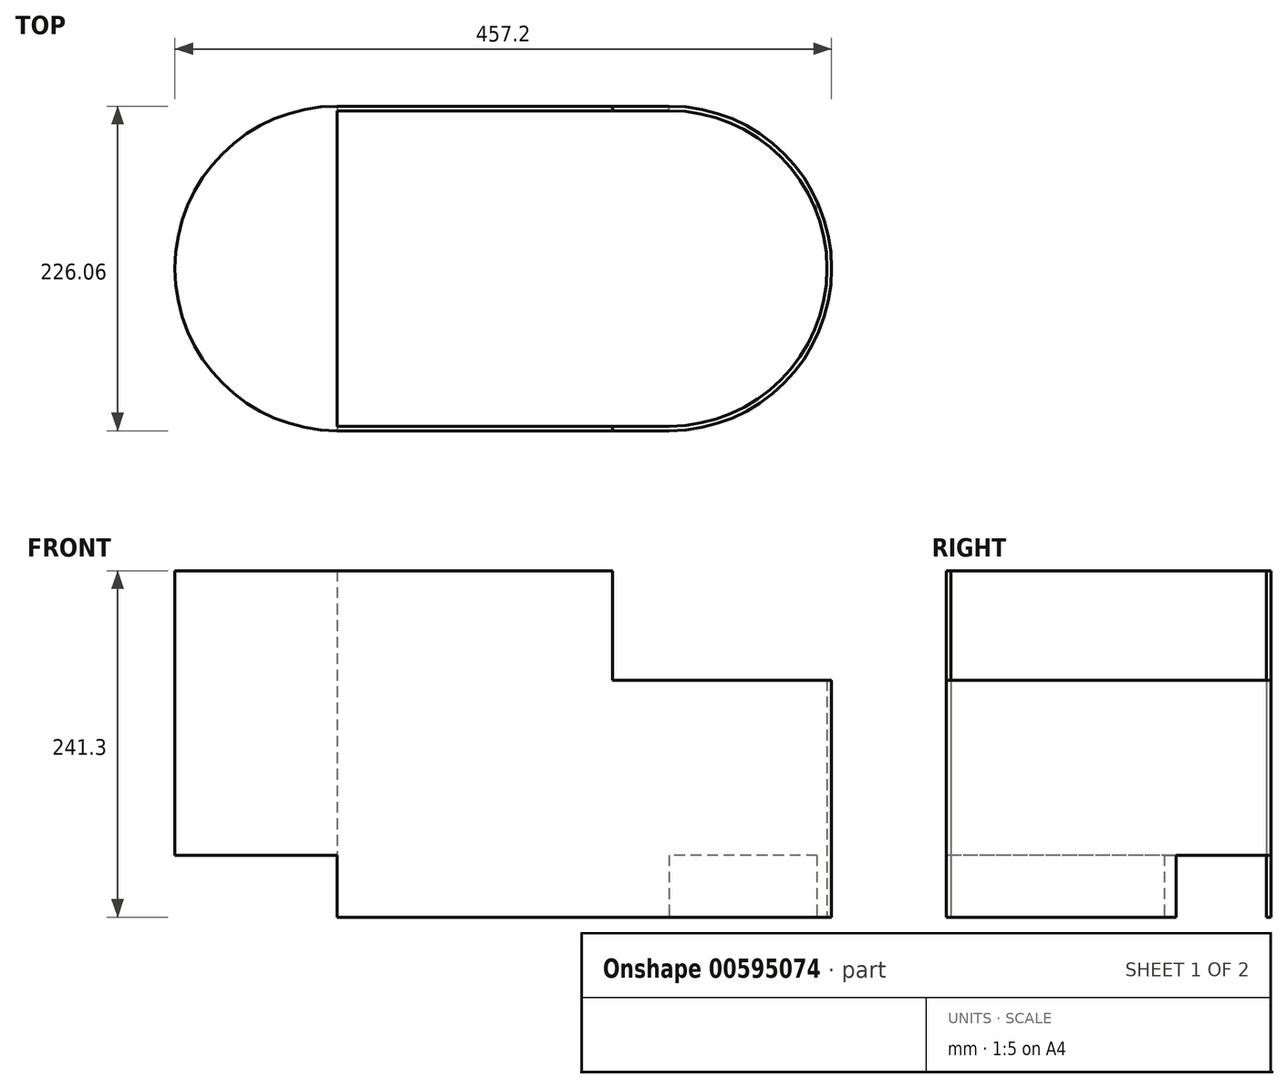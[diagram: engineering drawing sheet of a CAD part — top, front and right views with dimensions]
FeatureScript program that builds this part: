
annotation { "Feature Type Name" : "Feature", "Feature Type Description" : "" }
export const myFeature = defineFeature(function(context is Context, id is Id, definition is map)
    precondition{}
    {
        {
            var Q0;
            Q0=qCreatedBy(makeId("Top.planeOp"),FACE);
            var sketch = newSketch(context, id + "F0", { "sketchPlane" : qUnion([Q0])});
            skLineSegment(sketch, "E0.bottom", {"start": v(-173.03, 52.32) * mm, "end": v(58.1, 52.32) * mm});
            skLineSegment(sketch, "E0.top", {"start": v(-173.03, -173.74) * mm, "end": v(58.1, -173.74) * mm});
            skLineSegment(sketch, "E0.left", {"start": v(-173.03, 52.32) * mm, "end": v(-173.03, -173.74) * mm});
            skLineSegment(sketch, "E0.right", {"start": v(58.1, 52.32) * mm, "end": v(58.1, -173.74) * mm});
            skArc(sketch, "E1", {"start": v(58.1, -173.74) * mm, "mid": v(171.14, -60.71) * mm, "end": v(58.1, 52.32) * mm});
            skArc(sketch, "E2", {"start": v(-173.03, 52.32) * mm, "mid": v(-286.06, -60.71) * mm, "end": v(-173.03, -173.74) * mm});
            skPoint(sketch, "E3.endSnap0", {"position": v(-286.06, -60.71) * mm});
            skPoint(sketch, "E4.endSnap0", {"position": v(171.14, -60.71) * mm});
            skSolve(sketch);
        }
        {
            var Q0;
            Q0=makeQuery(id+"F0.imprint","IMPRINT",FACE,{"disambiguationData":[TD([[makeQuery(id+"F0.imprint","IMPRINT",EDGE,{"derivedFrom":sQuery(id+"F0.wireOp",EDGE,"E0.left")}),-1.0]])]});
            var Q1;
            Q1=makeQuery(id+"F0.imprint","IMPRINT",FACE,{"disambiguationData":[TD([[makeQuery(id+"F0.imprint","IMPRINT",EDGE,{"derivedFrom":sQuery(id+"F0.wireOp",EDGE,"E0.bottom")}),-1.0]])]});
            var Q2;
            Q2=makeQuery(id+"F0.imprint","IMPRINT",FACE,{"disambiguationData":[TD([[makeQuery(id+"F0.imprint","IMPRINT",EDGE,{"derivedFrom":sQuery(id+"F0.wireOp",EDGE,"E0.right")}),1.0]])]});
            var Q3;
            {var subQ0=sQuery(id+"F0.wireOp",EDGE,"E3");Q3=makeQuery(id+"F0.imprint","IMPRINT",FACE,{"disambiguationData":[TD([[makeQuery(id+"F0.imprint","IMPRINT",EDGE,{"derivedFrom":subQ0}),-1.0]])]});}
            var Q4;
            {var subQ0=sQuery(id+"F0.wireOp",EDGE,"E4");Q4=makeQuery(id+"F0.imprint","IMPRINT",FACE,{"disambiguationData":[TD([[makeQuery(id+"F0.imprint","IMPRINT",EDGE,{"derivedFrom":subQ0}),1.0]])]});}
            extrude(context, id + "F1", {"entities" : qUnion([Q0, Q1, Q2, Q3, Q4]), "depth" : 241.3 * mm, "offsetDistance" : 25.4 * mm});
        }
        {
            var Q0;
            Q0=makeQuery(id+"F1.opExtrude","SWEPT_FACE",FACE,{"disambiguationData":[OSD([sQuery(id+"F0.wireOp",EDGE,"E0.top"),sQuery(id+"F0.wireOp",EDGE,"E3")])]});
            var sketch = newSketch(context, id + "F2", { "sketchPlane" : qUnion([Q0])});
            skLineSegment(sketch, "E5", {"start": v(-286.06, 241.3) * mm, "end": v(-98.1, 241.3) * mm});
            skLineSegment(sketch, "E6", {"start": v(171.14, 241.3) * mm, "end": v(18.74, 241.3) * mm});
            skLineSegment(sketch, "E7", {"start": v(18.74, 241.3) * mm, "end": v(18.74, 0) * mm});
            skLineSegment(sketch, "E8", {"start": v(18.74, 241.3) * mm, "end": v(18.74, 165.1) * mm});
            skLineSegment(sketch, "E9", {"start": v(18.74, 165.1) * mm, "end": v(-82.86, 241.3) * mm});
            skLineSegment(sketch, "E10", {"start": v(18.74, 165.1) * mm, "end": v(171.14, 165.1) * mm});
            skLineSegment(sketch, "E11", {"start": v(171.14, 241.3) * mm, "end": v(171.14, 165.1) * mm});
            skLineSegment(sketch, "E12", {"start": v(18.74, 0) * mm, "end": v(18.74, 43.18) * mm});
            skLineSegment(sketch, "E13", {"start": v(18.74, 43.18) * mm, "end": v(-323.04, 43.18) * mm});
            skLineSegment(sketch, "E14", {"start": v(-323.04, 43.18) * mm, "end": v(-323.04, 0) * mm});
            skLineSegment(sketch, "E15", {"start": v(-323.04, 0) * mm, "end": v(18.74, 0) * mm});
            skSolve(sketch);
        }
        {
            var Q0;
            {var subQ0=sQuery(id+"F2.wireOp",EDGE,"E8");Q0=makeQuery(id+"F2.imprint","IMPRINT",FACE,{"disambiguationData":[TD([[makeQuery(id+"F2.imprint","IMPRINT",EDGE,{"derivedFrom":subQ0}),-1.0]])]});}
            var Q1;
            {var subQ0=sQuery(id+"F2.wireOp",EDGE,"E6");Q1=makeQuery(id+"F2.imprint","IMPRINT",FACE,{"disambiguationData":[TD([[makeQuery(id+"F2.imprint","IMPRINT",EDGE,{"derivedFrom":subQ0}),-1.0]])]});}
            var Q2;
            {var subQ3=sQuery(id+"F2.wireOp",EDGE,"E11");Q2=makeQuery(id+"F2.imprint","IMPRINT",FACE,{"disambiguationData":[TD([[makeQuery(id+"F2.imprint","IMPRINT",EDGE,{"derivedFrom":subQ3}),-1.0]])]});}
            var Q3;
            {var subQ0=sQuery(id+"F2.wireOp",EDGE,"E14");Q3=makeQuery(id+"F2.imprint","IMPRINT",FACE,{"disambiguationData":[TD([[makeQuery(id+"F2.imprint","IMPRINT",EDGE,{"derivedFrom":subQ0}),1.0]])]});}
            var Q4;
            {var subQ0=sQuery(id+"F2.wireOp",EDGE,"E12");Q4=makeQuery(id+"F2.imprint","IMPRINT",FACE,{"disambiguationData":[TD([[makeQuery(id+"F2.imprint","IMPRINT",EDGE,{"derivedFrom":subQ0}),1.0]])]});}
            extrude(context, id + "F3", {"entities" : qUnion([Q0, Q1, Q2, Q3, Q4]), "operationType" : NewBodyOperationType.REMOVE, "endBound" : BoundingType.THROUGH_ALL, "oppositeDirection" : true, "depth" : 25.4 * mm, "offsetDistance" : 25.4 * mm});
        }
        {
            var Q0;
            Q0=makeQuery(id+"F1.opExtrude","SWEPT_FACE",FACE,{"disambiguationData":[OSD([sQuery(id+"F0.wireOp",EDGE,"E0.bottom")])]});
            var sketch = newSketch(context, id + "F4", { "sketchPlane" : qUnion([Q0])});
            skLineSegment(sketch, "E16", {"start": v(-18.74, 43.18) * mm, "end": v(-160.98, 43.18) * mm});
            skLineSegment(sketch, "E17", {"start": v(-160.98, 43.18) * mm, "end": v(-160.98, 0) * mm});
            skLineSegment(sketch, "E18", {"start": v(-160.98, 0) * mm, "end": v(-18.74, 0) * mm});
            skSolve(sketch);
        }
        {
            var Q0;
            Q0=makeQuery(id+"F1.opExtrude","CAP_FACE",FACE,{"disambiguationData":[OSD([sQuery(id+"F0.wireOp",EDGE,"E0.bottom"),sQuery(id+"F0.wireOp",EDGE,"E0.top"),sQuery(id+"F0.wireOp",EDGE,"E1"),sQuery(id+"F0.wireOp",EDGE,"E2")])],"isStart":true});
            var sketch = newSketch(context, id + "F5", { "sketchPlane" : qUnion([Q0])});
            skLineSegment(sketch, "E19.0", {"start": v(-173.03, -49.14) * mm, "end": v(3.5, -49.14) * mm});
            skArc(sketch, "E19.1", {"start": v(-173.03, 170.57) * mm, "mid": v(-282.89, 60.71) * mm, "end": v(-173.03, -49.14) * mm});
            skLineSegment(sketch, "E19.2", {"start": v(3.5, 170.57) * mm, "end": v(-173.03, 170.57) * mm});
            skLineSegment(sketch, "E20.1", {"start": v(58.1, 170.57) * mm, "end": v(21.91, 170.57) * mm});
            skArc(sketch, "E20.2", {"start": v(58.1, -49.14) * mm, "mid": v(167.96, 60.71) * mm, "end": v(58.1, 170.57) * mm});
            skLineSegment(sketch, "E20.3", {"start": v(21.91, -49.14) * mm, "end": v(58.1, -49.14) * mm});
            skLineSegment(sketch, "E21", {"start": v(3.5, -49.14) * mm, "end": v(21.91, -49.14) * mm});
            skLineSegment(sketch, "E22", {"start": v(3.5, 170.57) * mm, "end": v(21.91, 170.57) * mm});
            skSolve(sketch);
        }
        {
            var Q0;
            {var subQ2=sQuery(id+"F5.wireOp",EDGE,"E19.0");Q0=makeQuery(id+"F5.imprint","IMPRINT",FACE,{"disambiguationData":[TD([[makeQuery(id+"F5.imprint","IMPRINT",EDGE,{"derivedFrom":subQ2}),1.0]])]});}
            var Q1;
            {var subQ6=sQuery(id+"F5.wireOp",EDGE,"E20.1");Q1=makeQuery(id+"F5.imprint","IMPRINT",FACE,{"disambiguationData":[TD([[makeQuery(id+"F5.imprint","IMPRINT",EDGE,{"derivedFrom":subQ6}),1.0]])]});}
            extrude(context, id + "F6", {"entities" : qUnion([Q0, Q1]), "operationType" : NewBodyOperationType.REMOVE, "endBound" : BoundingType.THROUGH_ALL, "oppositeDirection" : true, "depth" : 25.4 * mm, "offsetDistance" : 25.4 * mm});
        }
        {
            var Q0;
            {var subQ0=sQuery(id+"F4.wireOp",EDGE,"E17");Q0=makeQuery(id+"F4.imprint","IMPRINT",FACE,{"disambiguationData":[TD([[makeQuery(id+"F4.imprint","IMPRINT",EDGE,{"derivedFrom":subQ0}),1.0]])]});}
            var Q1;
            {var subQ1=sQuery(id+"F0.wireOp",EDGE,"E0.bottom");var subQ2=makeQuery(id+"F1.opExtrude","SWEPT_FACE",FACE,{"disambiguationData":[OSD([subQ1])]});var subQ3=makeQuery(id+"F3.boolean.opBoolean","INTERSECT",EDGE,{"derivedFrom":[subQ2,makeQuery(id+"F3.opExtrude","SWEPT_FACE",FACE,{"disambiguationData":[OSD([sQuery(id+"F2.wireOp",EDGE,"E12")])]})]});Q1=makeQuery(id+"F4.imprint","IMPRINT",FACE,{"disambiguationData":[TD([[makeQuery(id+"F4.imprint","IMPRINT",EDGE,{"derivedFrom":subQ3}),-1.0]])]});}
            extrude(context, id + "F7", {"entities" : qUnion([Q0, Q1]), "operationType" : NewBodyOperationType.REMOVE, "oppositeDirection" : true, "depth" : 114.05 * mm, "offsetDistance" : 25.4 * mm});
        }
    });
